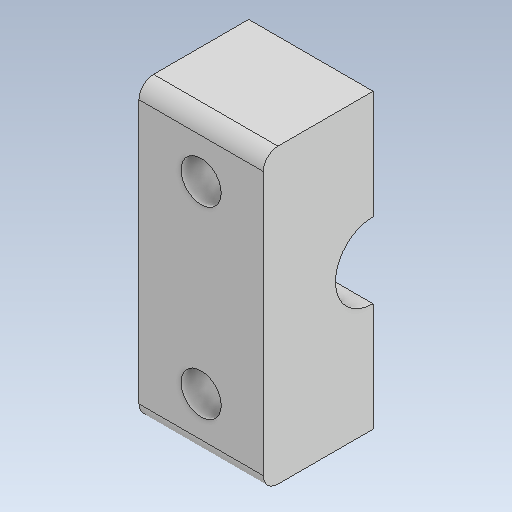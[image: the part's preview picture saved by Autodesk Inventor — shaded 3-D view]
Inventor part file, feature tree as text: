
AUTODESK INVENTOR PART (.ipt)
format: ipt  version: 2020 (Build 240168000, 168)  size: 120,832 bytes
history: native  units: mm
features: sketch x3, extrude x2, hole x1, fillet x1
ambient origin geometry x8: Origin, YZ Plane, XZ Plane, XY Plane, X Axis, Y Axis, Z Axis, Center Point
bodies: Solid1 (feature_tree)
feature tree (7):
  extrude  "Extrusion1"  Depth=17.0mm
  extrude  "Extrusion2"  Depth=15.0mm
  hole  "Hole1"  [1 undecoded]
  fillet  "Fillet1"  Radius=2.0mm
  sketch  "Sketch1"  dims[d0=40.0mm d1=17.0mm]
  sketch  "Sketch2"  dims[d2=15.0mm d3=0.0mm d5=10.3mm]
  sketch  "Sketch3"  dims[d6=0.0mm d7=0.0mm d8=0.0mm d9=5.5mm d10=6.0mm d11=4.0mm d12=2.0mm d13=90.0deg d14=8.0mm d15=20.594885mm d19=2.0mm]
note: 1 required parameter value undecoded (feature->parameter linkage not recoverable at this tier; creation-order binding heuristic only, values carry confidence <= 0.55)
